# Revit family: Drain_Floor_12_Inch_Square-Zurn-Z1805-12S
name_source: partatom
category: Plumbing Fixtures
units: mm (PartAtom-declared; Revit-internal decimal feet)

## family parameters
Always vertical = Yes
Cut with Voids When Loaded = No
Maintain Annotation Orientation = No
OmniClass Number = 23.45.55.21
OmniClass Title = Drains (Wastes)
Part Type = Normal
Room Calculation Point = No
Round Connector Dimension = Use Radius
Shared = No
Work Plane-Based = No

## types (18) — shared parameters
Assembly Code = D2030300
CW Connection = No
Default Elevation = 20 "
Description = 12” X 12” [305 X 305 ] SQUARE INDUSTRIAL HIGH CAPACITY SANITARY FLOOR DRAIN
HW Connection = No
Manufacturer = Zurn Water, LLC
Manufacurer Brand = Zurn
Modified Date = 02/18/2026
Product Documentation Link = https://files.zurn.com
Product Page URL = https://www.zurn.com
Product data url = https://bimobject.com
URL = www.zurn.com
Vent Connection = No
Waste Connection = Yes
zero-valued in all types: CWFU, HWFU, WFU

## per-type parameters (varying)
| type | Body Height  ' E ' | Main Material | Model | Pipe Size 'A' (Inner Diameter) | Pipe Size 'A' (Inner Radius) | Pipe Size 'A' (Nominal Diameter) | Pipe Size 'A' (Nominal Radius) | Pipe Size 'A' (Outer Diameter) | Pipe Size 'A' (Outer Radius) | Type Comments |
| Z1805-12S-3NH | 9.75 " | Steel - Zurn - Stainless - Type - 304 | Z1805-12S | 3.26 " | 1.63 " | 3 " | 1.5 " | 3.5 " | 1.75 " | Z1805-12S - 3 Inch No-Hub Outlet (Sch 10) |
| Z1805-12S-4NH | 9.656 " | Steel - Zurn - Stainless - Type - 304 | Z1805-12S | 4.26 " | 2.13 " | 4 " | 2 " | 4.5 " | 2.25 " | Z1805-12S - 4 Inch No-Hub Outlet (Sch 10) |
| Z1805-12S-6NH | 9.438 " | Steel - Zurn - Stainless - Type - 304 | Z1805-12S | 6.357 " | 3.179 " | 6 " | 3 " | 6.625 " | 3.313 " | Z1805-12S - 6 Inch No-Hub Outlet (Sch 10) |
| Z1805-12S-3BW | 9.75 " | Steel - Zurn - Stainless - Type - 304 | Z1805-12S | 3.26 " | 1.63 " | 3 " | 1.5 " | 3.5 " | 1.75 " | Z1805-12S - 3 Inch Butt-Weld Outlet (Sch 10) |
| Z1805-12S-4BW | 9.656 " | Steel - Zurn - Stainless - Type - 304 | Z1805-12S | 4.26 " | 2.13 " | 4 " | 2 " | 4.5 " | 2.25 " | Z1805-12S - 4 Inch Butt-Weld Outlet (Sch 10) |
| Z1805-12S-6BW | 9.438 " | Steel - Zurn - Stainless - Type - 304 | Z1805-12S | 6.357 " | 3.179 " | 6 " | 3 " | 6.625 " | 3.313 " | Z1805-12S - 6 Inch Butt-Weld Outlet (Sch 10) |
| Z1805-12S-3IP | 9.063 " | Steel - Zurn - Stainless - Type - 304 | Z1805-12S | 3.26 " | 1.63 " | 3 " | 1.5 " | 3.5 " | 1.75 " | Z1805-12S - 3 Inch IP Threaded Outlet |
| Z1805-12S-4IP | 9 " | Steel - Zurn - Stainless - Type - 304 | Z1805-12S | 4.26 " | 2.13 " | 4 " | 2 " | 4.5 " | 2.25 " | Z1805-12S - 4 Inch IP Threaded Outlet |
| Z1805-12S-6IP | 8.75 " | Steel - Zurn - Stainless - Type - 304 | Z1805-12S | 6.357 " | 3.179 " | 6 " | 3 " | 6.625 " | 3.313 " | Z1805-12S - 6 Inch IP Threaded Outlet |
| ZM1805-12S-3NH | 9.75 " | Steel - Zurn - Stainless - Type - 316 | ZM1805-12S | 3.26 " | 1.63 " | 3 " | 1.5 " | 3.5 " | 1.75 " | ZM1805-12S- 3 Inch No-Hub Outlet (Sch 10) |
| ZM1805-12S-4NH | 9.656 " | Steel - Zurn - Stainless - Type - 316 | ZM1805-12S | 4.26 " | 2.13 " | 4 " | 2 " | 4.5 " | 2.25 " | ZM1805-12S - 4 Inch No-Hub Outlet (Sch 10) |
| ZM1805-12S-6NH | 9.438 " | Steel - Zurn - Stainless - Type - 316 | ZM1805-12S | 6.357 " | 3.179 " | 6 " | 3 " | 6.625 " | 3.313 " | ZM1805-12S - 6 Inch No-Hub Outlet (Sch 10) |
| ZM1805-12S-3BW | 9.75 " | Steel - Zurn - Stainless - Type - 316 | ZM1805-12S | 3.26 " | 1.63 " | 3 " | 1.5 " | 3.5 " | 1.75 " | ZM1805-12S - 3 Inch Butt-Weld Outlet (Sch 10) |
| ZM1805-12S-4BW | 9.656 " | Steel - Zurn - Stainless - Type - 316 | ZM1805-12S | 4.26 " | 2.13 " | 4 " | 2 " | 4.5 " | 2.25 " | ZM1805-12S - 4 Inch Butt-Weld Outlet (Sch 10) |
| ZM1805-12S-6BW | 9.438 " | Steel - Zurn - Stainless - Type - 316 | ZM1805-12S | 6.357 " | 3.179 " | 6 " | 3 " | 6.625 " | 3.313 " | ZM1805-12S - 6 Inch Butt-Weld Outlet (Sch 10) |
| ZM1805-12S-3IP | 9.063 " | Steel - Zurn - Stainless - Type - 316 | ZM1805-12S | 3.26 " | 1.63 " | 3 " | 1.5 " | 3.5 " | 1.75 " | ZM1805-12S - 3 Inch IP Threaded Outlet |
| ZM1805-12S-4IP | 9 " | Steel - Zurn - Stainless - Type - 316 | ZM1805-12S | 4.26 " | 2.13 " | 4 " | 2 " | 4.5 " | 2.25 " | ZM1805-12S - 4 Inch IP Threaded Outlet |
| ZM1805-12S-6IP | 8.75 " | Steel - Zurn - Stainless - Type - 316 | ZM1805-12S | 6.357 " | 3.179 " | 6 " | 3 " | 6.625 " | 3.313 " | ZM1805-12S - 6 Inch IP Threaded Outlet |

## geometry (parser evidence)
native form markers: Blend x4, Sweep x2
no freeform markers — native parametric forms only
